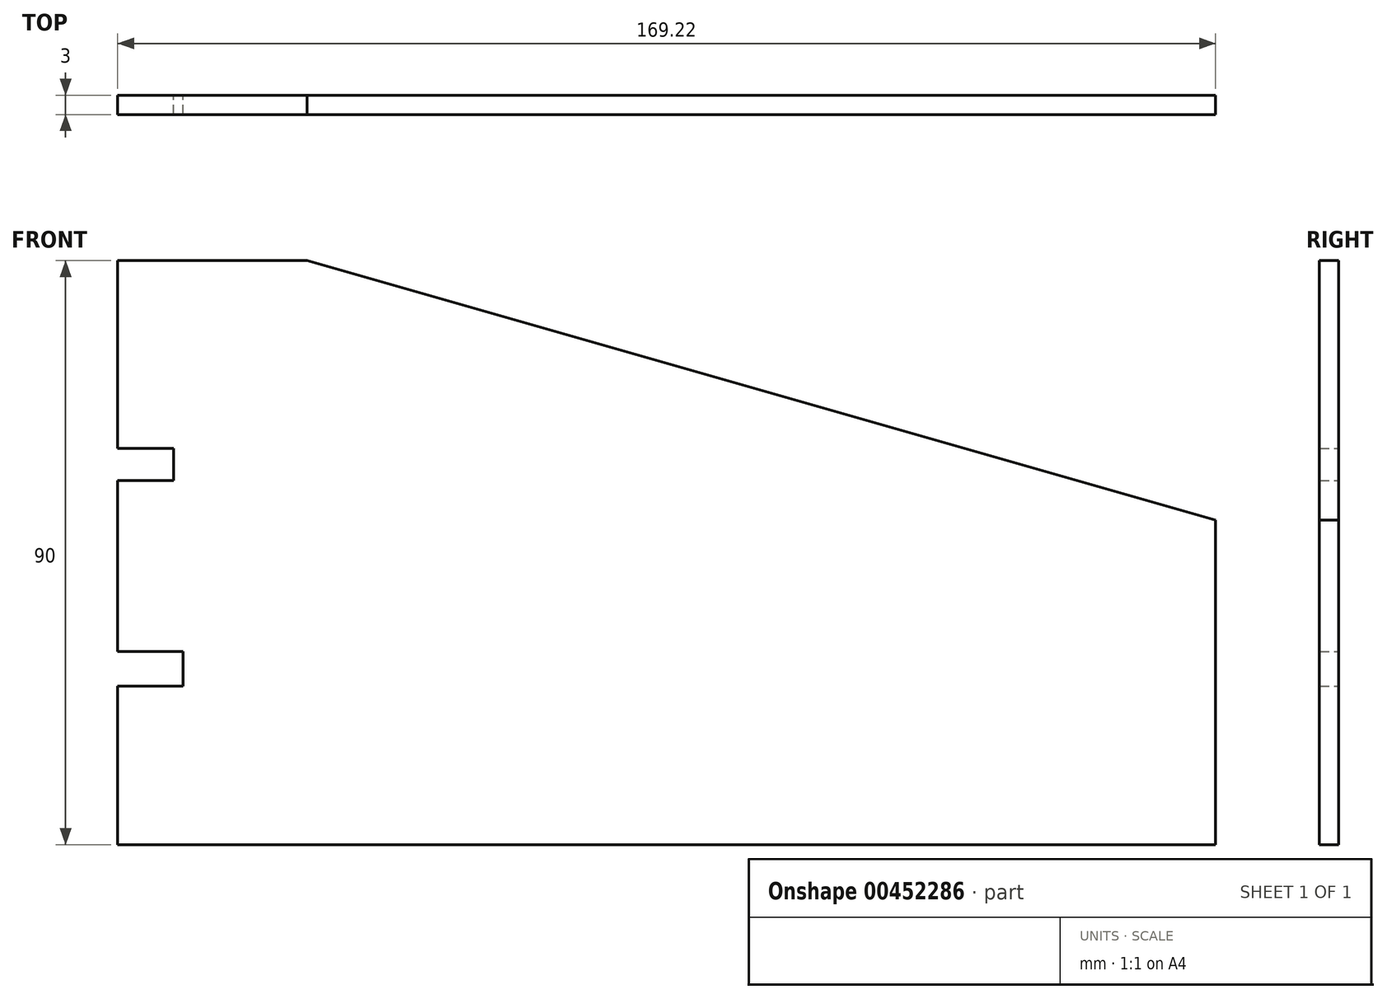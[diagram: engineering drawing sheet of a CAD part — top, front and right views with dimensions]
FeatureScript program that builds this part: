
annotation { "Feature Type Name" : "Feature", "Feature Type Description" : "" }
export const myFeature = defineFeature(function(context is Context, id is Id, definition is map)
    precondition{}
    {
        {
            var Q0;
            Q0=qCreatedBy(makeId("Front.planeOp"),FACE);
            var sketch = newSketch(context, id + "F0", { "sketchPlane" : qUnion([Q0])});
            skLineSegment(sketch, "E0.bottom", {"start": v(0, 0) * mm, "end": v(140, 0) * mm});
            skLineSegment(sketch, "E1", {"start": v(140, 0) * mm, "end": v(140, 50) * mm});
            skLineSegment(sketch, "E2", {"start": v(0, 90) * mm, "end": v(140, 50) * mm});
            skPoint(sketch, "E3.end.orphan", {"position": v(0, 27) * mm});
            skPoint(sketch, "E4.end.orphan", {"position": v(0, 57) * mm});
            skLineSegment(sketch, "E5.bottom", {"start": v(0, 90) * mm, "end": v(-29.22, 90) * mm});
            skLineSegment(sketch, "E5.top", {"start": v(0, 0) * mm, "end": v(-29.22, 0) * mm});
            skLineSegment(sketch, "E5.left", {"start": v(0, 60) * mm, "end": v(0, 57) * mm});
            skLineSegment(sketch, "E5.right", {"start": v(-29.22, 90) * mm, "end": v(-29.22, 61.08) * mm});
            skLineSegment(sketch, "E6.bottom", {"start": v(-29.22, 61.08) * mm, "end": v(-20.56, 61.08) * mm});
            skLineSegment(sketch, "E6.top", {"start": v(-29.22, 56.1) * mm, "end": v(-20.56, 56.1) * mm});
            skLineSegment(sketch, "E6.right", {"start": v(-20.56, 61.08) * mm, "end": v(-20.56, 56.1) * mm});
            skLineSegment(sketch, "E7.bottom", {"start": v(-29.22, 29.74) * mm, "end": v(-19.14, 29.74) * mm});
            skLineSegment(sketch, "E7.top", {"start": v(-29.22, 24.4) * mm, "end": v(-19.14, 24.4) * mm});
            skLineSegment(sketch, "E7.right", {"start": v(-19.14, 29.74) * mm, "end": v(-19.14, 24.4) * mm});
            skLineSegment(sketch, "E8.trimOffspring", {"start": v(-29.22, 56.1) * mm, "end": v(-29.22, 29.74) * mm});
            skLineSegment(sketch, "E9.trimOffspring", {"start": v(-29.22, 24.4) * mm, "end": v(-29.22, 0) * mm});
            skLineSegment(sketch, "E10.trimOffspring", {"start": v(0, 30) * mm, "end": v(0, 27) * mm});
            skSolve(sketch);
        }
        {
            var Q0;
            Q0 = qSketchRegion(id + "F0", true);
            extrude(context, id + "F1", {"entities" : qUnion([Q0]), "depth" : 3 * mm});
        }
    });
